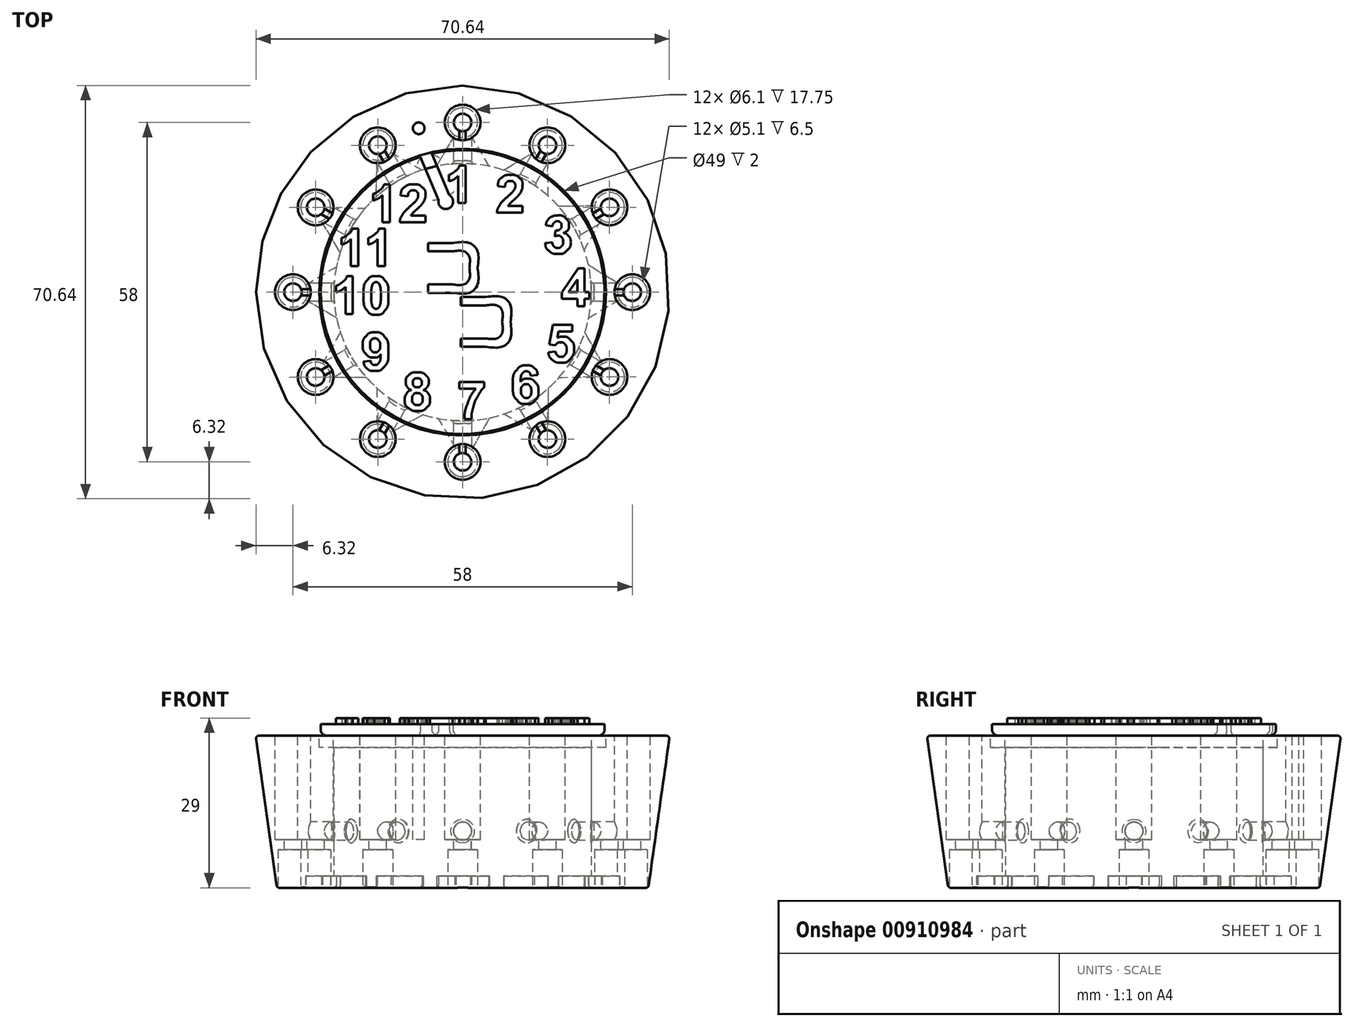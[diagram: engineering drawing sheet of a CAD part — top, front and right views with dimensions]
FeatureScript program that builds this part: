
annotation { "Feature Type Name" : "Feature", "Feature Type Description" : "" }
export const myFeature = defineFeature(function(context is Context, id is Id, definition is map)
    precondition{}
    {
        {
            var Q0;
            Q0=qCreatedBy(makeId("Front.planeOp"),FACE);
            var sketch = newSketch(context, id + "F0", { "sketchPlane" : qUnion([Q0])});
            skLineSegment(sketch, "E0.bottom", {"start": v(-22, 0) * mm, "end": v(-31.75, 0) * mm});
            skLineSegment(sketch, "E0.top", {"start": v(-22, 26) * mm, "end": v(-35.4, 26) * mm});
            skLineSegment(sketch, "E1", {"start": v(-35.4, 26) * mm, "end": v(-31.75, 0) * mm});
            skLineSegment(sketch, "E2", {"start": v(-30.25, 26.55) * mm, "end": v(-30.25, -4.35) * mm, "construction": true});
            skLineSegment(sketch, "E3", {"start": v(-22, 26) * mm, "end": v(-22, 0) * mm});
            skPoint(sketch, "E0.left.end.orphan", {"position": v(0, 26) * mm});
            skPoint(sketch, "E0.left.start.orphan", {"position": v(0, 0) * mm});
            skLineSegment(sketch, "E4", {"start": v(0, 0) * mm, "end": v(0, 33.66) * mm, "construction": true});
            skLineSegment(sketch, "E5", {"start": v(-29, 26) * mm, "end": v(-29, -2.92) * mm, "construction": true});
            skSolve(sketch);
        }
        {
            var Q0;
            Q0=makeQuery(id+"F0.imprint","IMPRINT",FACE,{"disambiguationData":[TD([[makeQuery(id+"F0.imprint","IMPRINT",EDGE,{"derivedFrom":sQuery(id+"F0.wireOp",EDGE,"E0.bottom")}),-1.0]])]});
            var Q1;
            Q1=sQuery(id+"F0.wireOp",EDGE,"E4");
            revolve(context, id + "F1", {"surfaceOperationType" : NewSurfaceOperationType.NEW, "entities" : qUnion([Q0]), "axis" : qUnion([Q1]), "revolveType" : RevolveType.FULL});
        }
        {
            var Q0;
            Q0=qCreatedBy(makeId("Top.planeOp"),FACE);
            cPlane(context, id + "F2", {"entities" : qUnion([Q0]), "cplaneType" : CPlaneType.OFFSET, "offset" : 26 * mm, "width" : 150 * mm, "height" : 150 * mm});
        }
        {
            var Q0;
            Q0=qCreatedBy(id+"F2.planeOp",FACE);
            var sketch = newSketch(context, id + "F3", { "sketchPlane" : qUnion([Q0])});
            skCircle(sketch, "E6", {"center": v(0, 0) * mm, "radius": 29 * mm, "construction": true});
            skLineSegment(sketch, "E7.0", {"start": v(-14.5, 25.11) * mm, "end": v(0, 29) * mm, "construction": true});
            skLineSegment(sketch, "E7.1", {"start": v(0, 29) * mm, "end": v(14.5, 25.11) * mm, "construction": true});
            skLineSegment(sketch, "E7.2", {"start": v(14.5, 25.11) * mm, "end": v(25.11, 14.5) * mm, "construction": true});
            skLineSegment(sketch, "E7.3", {"start": v(25.11, 14.5) * mm, "end": v(29, 0) * mm, "construction": true});
            skLineSegment(sketch, "E7.4", {"start": v(29, 0) * mm, "end": v(25.11, -14.5) * mm, "construction": true});
            skLineSegment(sketch, "E7.5", {"start": v(25.11, -14.5) * mm, "end": v(14.5, -25.11) * mm, "construction": true});
            skLineSegment(sketch, "E7.6", {"start": v(14.5, -25.11) * mm, "end": v(0, -29) * mm, "construction": true});
            skLineSegment(sketch, "E7.7", {"start": v(0, -29) * mm, "end": v(-14.5, -25.11) * mm, "construction": true});
            skLineSegment(sketch, "E7.8", {"start": v(-14.5, -25.11) * mm, "end": v(-25.11, -14.5) * mm, "construction": true});
            skLineSegment(sketch, "E7.9", {"start": v(-25.11, -14.5) * mm, "end": v(-29, 0) * mm, "construction": true});
            skLineSegment(sketch, "E7.10", {"start": v(-29, 0) * mm, "end": v(-25.11, 14.5) * mm, "construction": true});
            skLineSegment(sketch, "E7.11", {"start": v(-25.11, 14.5) * mm, "end": v(-14.5, 25.11) * mm, "construction": true});
            skCircle(sketch, "E8", {"center": v(0, 29) * mm, "radius": 3.05 * mm});
            skCircle(sketch, "E9", {"center": v(14.5, 25.11) * mm, "radius": 3.05 * mm});
            skCircle(sketch, "E10", {"center": v(-14.5, 25.11) * mm, "radius": 3.05 * mm});
            skCircle(sketch, "E11", {"center": v(-25.11, 14.5) * mm, "radius": 3.05 * mm});
            skCircle(sketch, "E12", {"center": v(25.11, 14.5) * mm, "radius": 3.05 * mm});
            skCircle(sketch, "E13", {"center": v(-29, 0) * mm, "radius": 3.05 * mm});
            skCircle(sketch, "E14", {"center": v(-25.11, -14.5) * mm, "radius": 3.05 * mm});
            skCircle(sketch, "E15", {"center": v(-14.5, -25.11) * mm, "radius": 3.05 * mm});
            skCircle(sketch, "E16", {"center": v(0, -29) * mm, "radius": 3.05 * mm});
            skCircle(sketch, "E17", {"center": v(14.5, -25.11) * mm, "radius": 3.05 * mm});
            skCircle(sketch, "E18", {"center": v(25.11, -14.5) * mm, "radius": 3.05 * mm});
            skCircle(sketch, "E19", {"center": v(29, 0) * mm, "radius": 3.05 * mm});
            skCircle(sketch, "E20", {"center": v(-7.5, 28.01) * mm, "radius": 1 * mm});
            skArc(sketch, "E21", {"start": v(0, 29) * mm, "mid": v(-7.5, 28.01) * mm, "end": v(-14.5, 25.11) * mm, "construction": true});
            skLineSegment(sketch, "E22.0", {"start": v(0.3, 24.24) * mm, "end": v(14.5, 25.11) * mm, "construction": true});
            skLineSegment(sketch, "E22.1", {"start": v(0.3, 24.24) * mm, "end": v(0, 29) * mm, "construction": true});
            skSolve(sketch);
        }
        {
            var Q0;
            Q0 = qSketchRegion(id + "F3", true);
            extrude(context, id + "F4", {"entities" : qUnion([Q0]), "operationType" : NewBodyOperationType.REMOVE, "oppositeDirection" : true, "depth" : 17.75 * mm, "offsetDistance" : 25 * mm});
        }
        {
            var Q0;
            Q0=qCreatedBy(makeId("Top.planeOp"),FACE);
            var sketch = newSketch(context, id + "F5", { "sketchPlane" : qUnion([Q0])});
            skCircle(sketch, "E23.cCircle", {"center": v(0, 0) * mm, "radius": 29 * mm, "construction": true});
            skLineSegment(sketch, "E23.0", {"start": v(0, -29) * mm, "end": v(-14.5, -25.11) * mm, "construction": true});
            skLineSegment(sketch, "E23.1", {"start": v(-14.5, -25.11) * mm, "end": v(-25.11, -14.5) * mm, "construction": true});
            skLineSegment(sketch, "E23.2", {"start": v(-25.11, -14.5) * mm, "end": v(-29, 0) * mm, "construction": true});
            skLineSegment(sketch, "E23.3", {"start": v(-29, 0) * mm, "end": v(-25.11, 14.5) * mm, "construction": true});
            skLineSegment(sketch, "E23.4", {"start": v(-25.11, 14.5) * mm, "end": v(-14.5, 25.11) * mm, "construction": true});
            skLineSegment(sketch, "E23.5", {"start": v(-14.5, 25.11) * mm, "end": v(0, 29) * mm, "construction": true});
            skLineSegment(sketch, "E23.6", {"start": v(0, 29) * mm, "end": v(14.5, 25.11) * mm, "construction": true});
            skLineSegment(sketch, "E23.7", {"start": v(14.5, 25.11) * mm, "end": v(25.11, 14.5) * mm, "construction": true});
            skLineSegment(sketch, "E23.8", {"start": v(25.11, 14.5) * mm, "end": v(29, 0) * mm, "construction": true});
            skLineSegment(sketch, "E23.9", {"start": v(29, 0) * mm, "end": v(25.11, -14.5) * mm, "construction": true});
            skLineSegment(sketch, "E23.10", {"start": v(25.11, -14.5) * mm, "end": v(14.5, -25.11) * mm, "construction": true});
            skLineSegment(sketch, "E23.11", {"start": v(14.5, -25.11) * mm, "end": v(0, -29) * mm, "construction": true});
            skCircle(sketch, "E24", {"center": v(0, -29) * mm, "radius": 2.55 * mm});
            skCircle(sketch, "E25", {"center": v(14.5, -25.11) * mm, "radius": 2.55 * mm});
            skCircle(sketch, "E26", {"center": v(-14.5, -25.11) * mm, "radius": 2.55 * mm});
            skCircle(sketch, "E27", {"center": v(25.11, -14.5) * mm, "radius": 2.55 * mm});
            skCircle(sketch, "E28", {"center": v(-25.11, -14.5) * mm, "radius": 2.55 * mm});
            skCircle(sketch, "E29", {"center": v(0, 29) * mm, "radius": 2.55 * mm});
            skCircle(sketch, "E30", {"center": v(-14.5, 25.11) * mm, "radius": 2.55 * mm});
            skCircle(sketch, "E31", {"center": v(14.5, 25.11) * mm, "radius": 2.55 * mm});
            skCircle(sketch, "E32", {"center": v(25.11, 14.5) * mm, "radius": 2.55 * mm});
            skCircle(sketch, "E33", {"center": v(29, 0) * mm, "radius": 2.55 * mm});
            skCircle(sketch, "E34", {"center": v(-25.11, 14.5) * mm, "radius": 2.55 * mm});
            skCircle(sketch, "E35", {"center": v(-29, 0) * mm, "radius": 2.55 * mm});
            skSolve(sketch);
        }
        {
            var Q0;
            Q0 = qSketchRegion(id + "F5", true);
            extrude(context, id + "F6", {"entities" : qUnion([Q0]), "operationType" : NewBodyOperationType.REMOVE, "depth" : 6.5 * mm, "offsetDistance" : 25 * mm});
        }
        {
            var Q0;
            Q0=qCreatedBy(id+"F2.planeOp",FACE);
            var sketch = newSketch(context, id + "F7", { "sketchPlane" : qUnion([Q0])});
            skCircle(sketch, "E36.cCircle", {"center": v(0, 0) * mm, "radius": 29 * mm, "construction": true});
            skLineSegment(sketch, "E36.0", {"start": v(0, 29) * mm, "end": v(14.5, 25.11) * mm, "construction": true});
            skLineSegment(sketch, "E36.1", {"start": v(14.5, 25.11) * mm, "end": v(25.12, 14.5) * mm, "construction": true});
            skLineSegment(sketch, "E36.2", {"start": v(25.12, 14.5) * mm, "end": v(29, 0) * mm, "construction": true});
            skLineSegment(sketch, "E36.3", {"start": v(29, 0) * mm, "end": v(25.11, -14.5) * mm, "construction": true});
            skLineSegment(sketch, "E36.4", {"start": v(25.11, -14.5) * mm, "end": v(14.5, -25.12) * mm, "construction": true});
            skLineSegment(sketch, "E36.5", {"start": v(14.5, -25.12) * mm, "end": v(0, -29) * mm, "construction": true});
            skLineSegment(sketch, "E36.6", {"start": v(0, -29) * mm, "end": v(-14.5, -25.11) * mm, "construction": true});
            skLineSegment(sketch, "E36.7", {"start": v(-14.5, -25.11) * mm, "end": v(-25.12, -14.5) * mm, "construction": true});
            skLineSegment(sketch, "E36.8", {"start": v(-25.12, -14.5) * mm, "end": v(-29, 0) * mm, "construction": true});
            skLineSegment(sketch, "E36.9", {"start": v(-29, 0) * mm, "end": v(-25.11, 14.5) * mm, "construction": true});
            skLineSegment(sketch, "E36.10", {"start": v(-25.11, 14.5) * mm, "end": v(-14.5, 25.12) * mm, "construction": true});
            skLineSegment(sketch, "E36.11", {"start": v(-14.5, 25.12) * mm, "end": v(0, 29) * mm, "construction": true});
            skCircle(sketch, "E37", {"center": v(14.5, 25.11) * mm, "radius": 1.5 * mm});
            skCircle(sketch, "E38", {"center": v(-14.5, 25.12) * mm, "radius": 1.5 * mm});
            skCircle(sketch, "E39", {"center": v(25.12, 14.5) * mm, "radius": 1.5 * mm});
            skCircle(sketch, "E40", {"center": v(0, 29) * mm, "radius": 1.5 * mm});
            skCircle(sketch, "E41", {"center": v(-25.11, 14.5) * mm, "radius": 1.5 * mm});
            skCircle(sketch, "E42", {"center": v(-29, 0) * mm, "radius": 1.5 * mm});
            skCircle(sketch, "E43", {"center": v(-25.12, -14.5) * mm, "radius": 1.5 * mm});
            skCircle(sketch, "E44", {"center": v(-14.5, -25.11) * mm, "radius": 1.5 * mm});
            skCircle(sketch, "E45", {"center": v(0, -29) * mm, "radius": 1.5 * mm});
            skCircle(sketch, "E46", {"center": v(14.5, -25.12) * mm, "radius": 1.5 * mm});
            skCircle(sketch, "E47", {"center": v(25.11, -14.5) * mm, "radius": 1.5 * mm});
            skCircle(sketch, "E48", {"center": v(29, 0) * mm, "radius": 1.5 * mm});
            skSolve(sketch);
        }
        {
            var Q0;
            Q0 = qSketchRegion(id + "F7", true);
            extrude(context, id + "F8", {"entities" : qUnion([Q0]), "operationType" : NewBodyOperationType.REMOVE, "oppositeDirection" : true, "depth" : 30 * mm, "offsetDistance" : 25 * mm});
        }
        {
            var Q0;
            Q0=qCreatedBy(makeId("Right.planeOp"),FACE);
            var sketch = newSketch(context, id + "F9", { "sketchPlane" : qUnion([Q0])});
            skCircle(sketch, "E49", {"center": v(0, 9.7) * mm, "radius": 1.55 * mm});
            skSolve(sketch);
        }
        {
            var Q0;
            Q0=makeQuery(id+"F9.imprint","IMPRINT",FACE,{"disambiguationData":[TD([[makeQuery(id+"F9.imprint","IMPRINT",EDGE,{"derivedFrom":sQuery(id+"F9.wireOp",EDGE,"E49")}),1.0]])]});
            extrude(context, id + "F10", {"entities" : qUnion([Q0]), "operationType" : NewBodyOperationType.REMOVE, "depth" : 29 * mm, "offsetDistance" : 25 * mm, "hasSecondDirection" : true, "secondDirectionOppositeDirection" : true, "secondDirectionDepth" : 29 * mm});
        }
        {
            var Q0;
            Q0=qCreatedBy(makeId("Front.planeOp"),FACE);
            var sketch = newSketch(context, id + "F11", { "sketchPlane" : qUnion([Q0])});
            skCircle(sketch, "E50", {"center": v(0, 9.7) * mm, "radius": 1.55 * mm});
            skSolve(sketch);
        }
        {
            var Q0;
            Q0=makeQuery(id+"F11.imprint","IMPRINT",FACE,{"disambiguationData":[TD([[makeQuery(id+"F11.imprint","IMPRINT",EDGE,{"derivedFrom":sQuery(id+"F11.wireOp",EDGE,"E50")}),1.0]])]});
            var Q1;
            Q1=sQuery(id+"F11.wireOp",EDGE,"E50");
            extrude(context, id + "F12", {"entities" : qUnion([Q0]), "operationType" : NewBodyOperationType.REMOVE, "surfaceEntities" : qUnion([Q1]), "oppositeDirection" : true, "depth" : 29 * mm, "offsetDistance" : 25 * mm, "hasSecondDirection" : true, "secondDirectionOppositeDirection" : false, "secondDirectionDepth" : 29 * mm});
        }
        {
            var Q0;
            Q0=makeQuery(id+"F1.opRevolve","SWEPT_FACE",FACE,{"disambiguationData":[OSD([sQuery(id+"F0.wireOp",EDGE,"E3")])]});
            cPlane(context, id + "F13", {"entities" : qUnion([Q0]), "cplaneType" : CPlaneType.LINE_ANGLE, "offset" : 25 * mm, "angle" : 60 * degree, "width" : 150 * mm, "height" : 150 * mm});
        }
        {
            var Q0;
            Q0=makeQuery(id+"F1.opRevolve","SWEPT_FACE",FACE,{"disambiguationData":[OSD([sQuery(id+"F0.wireOp",EDGE,"E1")])]});
            cPlane(context, id + "F14", {"entities" : qUnion([Q0]), "cplaneType" : CPlaneType.LINE_ANGLE, "offset" : 25 * mm, "angle" : 30 * degree, "width" : 150 * mm, "height" : 150 * mm});
        }
        {
            var Q0;
            Q0=qCreatedBy(id+"F13.planeOp",FACE);
            var sketch = newSketch(context, id + "F15", { "sketchPlane" : qUnion([Q0])});
            skCircle(sketch, "E51", {"center": v(0, 9.7) * mm, "radius": 1.55 * mm});
            skSolve(sketch);
        }
        {
            var Q0;
            Q0=makeQuery(id+"F15.imprint","IMPRINT",FACE,{"disambiguationData":[TD([[makeQuery(id+"F15.imprint","IMPRINT",EDGE,{"derivedFrom":sQuery(id+"F15.wireOp",EDGE,"E51")}),1.0]])]});
            var Q1;
            Q1=sQuery(id+"F15.wireOp",EDGE,"E51");
            extrude(context, id + "F16", {"entities" : qUnion([Q0]), "operationType" : NewBodyOperationType.REMOVE, "surfaceEntities" : qUnion([Q1]), "oppositeDirection" : true, "depth" : 29 * mm, "offsetDistance" : 25 * mm, "hasSecondDirection" : true, "secondDirectionOppositeDirection" : false, "secondDirectionDepth" : 29 * mm});
        }
        {
            var Q0;
            Q0=qCreatedBy(id+"F14.planeOp",FACE);
            var sketch = newSketch(context, id + "F17", { "sketchPlane" : qUnion([Q0])});
            skCircle(sketch, "E52", {"center": v(0, 9.7) * mm, "radius": 1.55 * mm});
            skSolve(sketch);
        }
        {
            var Q0;
            Q0=makeQuery(id+"F17.imprint","IMPRINT",FACE,{"disambiguationData":[TD([[makeQuery(id+"F17.imprint","IMPRINT",EDGE,{"derivedFrom":sQuery(id+"F17.wireOp",EDGE,"E52")}),1.0]])]});
            var Q1;
            Q1=sQuery(id+"F17.wireOp",EDGE,"E52");
            extrude(context, id + "F18", {"entities" : qUnion([Q0]), "operationType" : NewBodyOperationType.REMOVE, "surfaceEntities" : qUnion([Q1]), "oppositeDirection" : true, "depth" : 29 * mm, "offsetDistance" : 25 * mm, "hasSecondDirection" : true, "secondDirectionOppositeDirection" : false, "secondDirectionDepth" : 29 * mm});
        }
        {
            var Q0;
            Q0=makeQuery(id+"F1.opRevolve","SWEPT_FACE",FACE,{"disambiguationData":[OSD([sQuery(id+"F0.wireOp",EDGE,"E1")])]});
            cPlane(context, id + "F19", {"entities" : qUnion([Q0]), "cplaneType" : CPlaneType.LINE_ANGLE, "offset" : 25 * mm, "angle" : 30 * degree, "oppositeDirection" : true, "width" : 150 * mm, "height" : 150 * mm});
        }
        {
            var Q0;
            Q0=makeQuery(id+"F1.opRevolve","SWEPT_FACE",FACE,{"disambiguationData":[OSD([sQuery(id+"F0.wireOp",EDGE,"E1")])]});
            cPlane(context, id + "F20", {"entities" : qUnion([Q0]), "cplaneType" : CPlaneType.LINE_ANGLE, "offset" : 25 * mm, "angle" : 60 * degree, "oppositeDirection" : true, "width" : 150 * mm, "height" : 150 * mm});
        }
        {
            var Q0;
            Q0=qCreatedBy(id+"F19.planeOp",FACE);
            var sketch = newSketch(context, id + "F21", { "sketchPlane" : qUnion([Q0])});
            skCircle(sketch, "E53", {"center": v(0, 9.7) * mm, "radius": 1.55 * mm});
            skSolve(sketch);
        }
        {
            var Q0;
            Q0=qCreatedBy(id+"F20.planeOp",FACE);
            var sketch = newSketch(context, id + "F22", { "sketchPlane" : qUnion([Q0])});
            skCircle(sketch, "E54", {"center": v(0, 9.7) * mm, "radius": 1.55 * mm});
            skSolve(sketch);
        }
        {
            var Q0;
            Q0 = qSketchRegion(id + "F22", true);
            extrude(context, id + "F23", {"entities" : qUnion([Q0]), "operationType" : NewBodyOperationType.REMOVE, "oppositeDirection" : true, "depth" : 29 * mm, "offsetDistance" : 25 * mm, "hasSecondDirection" : true, "secondDirectionOppositeDirection" : false, "secondDirectionDepth" : 29 * mm});
        }
        {
            var Q0;
            Q0 = qSketchRegion(id + "F21", true);
            extrude(context, id + "F24", {"entities" : qUnion([Q0]), "operationType" : NewBodyOperationType.REMOVE, "oppositeDirection" : true, "depth" : 29 * mm, "offsetDistance" : 25 * mm, "hasSecondDirection" : true, "secondDirectionOppositeDirection" : false, "secondDirectionDepth" : 29 * mm});
        }
        {
            var Q0;
            Q0=qCreatedBy(id+"F2.planeOp",FACE);
            var sketch = newSketch(context, id + "F25", { "sketchPlane" : qUnion([Q0])});
            skCircle(sketch, "E55", {"center": v(0, 0) * mm, "radius": 24.5 * mm});
            skSolve(sketch);
        }
        {
            var Q0;
            Q0 = qSketchRegion(id + "F25", true);
            extrude(context, id + "F26", {"entities" : qUnion([Q0]), "operationType" : NewBodyOperationType.REMOVE, "oppositeDirection" : true, "depth" : 2 * mm, "offsetDistance" : 25 * mm});
        }
        {
            var Q0;
            Q0=makeQuery(id+"F6.boolean.opBoolean","COPY",EDGE,{"derivedFrom":makeQuery(id+"F6.opExtrude","CAP_EDGE",EDGE,{"disambiguationData":[OSD([sQuery(id+"F5.wireOp",EDGE,"E27")])],"isStart":true})});
            var Q1;
            Q1=makeQuery(id+"F6.boolean.opBoolean","COPY",EDGE,{"derivedFrom":makeQuery(id+"F6.opExtrude","CAP_EDGE",EDGE,{"disambiguationData":[OSD([sQuery(id+"F5.wireOp",EDGE,"E25")])],"isStart":true})});
            var Q2;
            Q2=makeQuery(id+"F1.opRevolve","SWEPT_EDGE",EDGE,{"disambiguationData":[OSD([sQuery(id+"F0.wireOp",EDGE,"E0.bottom"),sQuery(id+"F0.wireOp",EDGE,"E1")])]});
            var Q3;
            Q3=makeQuery(id+"F6.boolean.opBoolean","COPY",EDGE,{"derivedFrom":makeQuery(id+"F6.opExtrude","CAP_EDGE",EDGE,{"disambiguationData":[OSD([sQuery(id+"F5.wireOp",EDGE,"E32")])],"isStart":true})});
            var Q4;
            Q4=makeQuery(id+"F6.boolean.opBoolean","COPY",EDGE,{"derivedFrom":makeQuery(id+"F6.opExtrude","CAP_EDGE",EDGE,{"disambiguationData":[OSD([sQuery(id+"F5.wireOp",EDGE,"E33")])],"isStart":true})});
            var Q5;
            Q5=makeQuery(id+"F6.boolean.opBoolean","COPY",EDGE,{"derivedFrom":makeQuery(id+"F6.opExtrude","CAP_EDGE",EDGE,{"disambiguationData":[OSD([sQuery(id+"F5.wireOp",EDGE,"E31")])],"isStart":true})});
            var Q6;
            Q6=makeQuery(id+"F6.boolean.opBoolean","COPY",EDGE,{"derivedFrom":makeQuery(id+"F6.opExtrude","CAP_EDGE",EDGE,{"disambiguationData":[OSD([sQuery(id+"F5.wireOp",EDGE,"E29")])],"isStart":true})});
            var Q7;
            Q7=makeQuery(id+"F6.boolean.opBoolean","COPY",EDGE,{"derivedFrom":makeQuery(id+"F6.opExtrude","CAP_EDGE",EDGE,{"disambiguationData":[OSD([sQuery(id+"F5.wireOp",EDGE,"E30")])],"isStart":true})});
            var Q8;
            Q8=makeQuery(id+"F6.boolean.opBoolean","COPY",EDGE,{"derivedFrom":makeQuery(id+"F6.opExtrude","CAP_EDGE",EDGE,{"disambiguationData":[OSD([sQuery(id+"F5.wireOp",EDGE,"E34")])],"isStart":true})});
            var Q9;
            Q9=makeQuery(id+"F6.boolean.opBoolean","COPY",EDGE,{"derivedFrom":makeQuery(id+"F6.opExtrude","CAP_EDGE",EDGE,{"disambiguationData":[OSD([sQuery(id+"F5.wireOp",EDGE,"E35")])],"isStart":true})});
            var Q10;
            Q10=makeQuery(id+"F6.boolean.opBoolean","COPY",EDGE,{"derivedFrom":makeQuery(id+"F6.opExtrude","CAP_EDGE",EDGE,{"disambiguationData":[OSD([sQuery(id+"F5.wireOp",EDGE,"E28")])],"isStart":true})});
            var Q11;
            Q11=makeQuery(id+"F6.boolean.opBoolean","COPY",EDGE,{"derivedFrom":makeQuery(id+"F6.opExtrude","CAP_EDGE",EDGE,{"disambiguationData":[OSD([sQuery(id+"F5.wireOp",EDGE,"E26")])],"isStart":true})});
            var Q12;
            Q12=makeQuery(id+"F6.boolean.opBoolean","COPY",EDGE,{"derivedFrom":makeQuery(id+"F6.opExtrude","CAP_EDGE",EDGE,{"disambiguationData":[OSD([sQuery(id+"F5.wireOp",EDGE,"E24")])],"isStart":true})});
            var Q13;
            Q13=makeQuery(id+"F1.opRevolve","SWEPT_EDGE",EDGE,{"disambiguationData":[OSD([sQuery(id+"F0.wireOp",EDGE,"E0.bottom"),sQuery(id+"F0.wireOp",EDGE,"E3")])]});
            var Q14;
            Q14=makeQuery(id+"F1.opRevolve","SWEPT_EDGE",EDGE,{"disambiguationData":[OSD([sQuery(id+"F0.wireOp",EDGE,"E0.top"),sQuery(id+"F0.wireOp",EDGE,"E1")])]});
            var Q15;
            Q15=makeQuery(id+"F4.boolean.opBoolean","COPY",EDGE,{"derivedFrom":makeQuery(id+"F4.opExtrude","CAP_EDGE",EDGE,{"disambiguationData":[OSD([sQuery(id+"F3.wireOp",EDGE,"E15")])],"isStart":true})});
            var Q16;
            Q16=makeQuery(id+"F4.boolean.opBoolean","COPY",EDGE,{"derivedFrom":makeQuery(id+"F4.opExtrude","CAP_EDGE",EDGE,{"disambiguationData":[OSD([sQuery(id+"F3.wireOp",EDGE,"E14")])],"isStart":true})});
            var Q17;
            Q17=makeQuery(id+"F4.boolean.opBoolean","COPY",EDGE,{"derivedFrom":makeQuery(id+"F4.opExtrude","CAP_EDGE",EDGE,{"disambiguationData":[OSD([sQuery(id+"F3.wireOp",EDGE,"E16")])],"isStart":true})});
            var Q18;
            Q18=makeQuery(id+"F4.boolean.opBoolean","COPY",EDGE,{"derivedFrom":makeQuery(id+"F4.opExtrude","CAP_EDGE",EDGE,{"disambiguationData":[OSD([sQuery(id+"F3.wireOp",EDGE,"E17")])],"isStart":true})});
            var Q19;
            Q19=makeQuery(id+"F4.boolean.opBoolean","COPY",EDGE,{"derivedFrom":makeQuery(id+"F4.opExtrude","CAP_EDGE",EDGE,{"disambiguationData":[OSD([sQuery(id+"F3.wireOp",EDGE,"E18")])],"isStart":true})});
            var Q20;
            Q20=makeQuery(id+"F4.boolean.opBoolean","COPY",EDGE,{"derivedFrom":makeQuery(id+"F4.opExtrude","CAP_EDGE",EDGE,{"disambiguationData":[OSD([sQuery(id+"F3.wireOp",EDGE,"E19")])],"isStart":true})});
            var Q21;
            Q21=makeQuery(id+"F4.boolean.opBoolean","COPY",EDGE,{"derivedFrom":makeQuery(id+"F4.opExtrude","CAP_EDGE",EDGE,{"disambiguationData":[OSD([sQuery(id+"F3.wireOp",EDGE,"E12")])],"isStart":true})});
            var Q22;
            Q22=makeQuery(id+"F4.boolean.opBoolean","COPY",EDGE,{"derivedFrom":makeQuery(id+"F4.opExtrude","CAP_EDGE",EDGE,{"disambiguationData":[OSD([sQuery(id+"F3.wireOp",EDGE,"E10")])],"isStart":true})});
            var Q23;
            Q23=makeQuery(id+"F4.boolean.opBoolean","COPY",EDGE,{"derivedFrom":makeQuery(id+"F4.opExtrude","CAP_EDGE",EDGE,{"disambiguationData":[OSD([sQuery(id+"F3.wireOp",EDGE,"E9")])],"isStart":true})});
            var Q24;
            Q24=makeQuery(id+"F4.boolean.opBoolean","COPY",EDGE,{"derivedFrom":makeQuery(id+"F4.opExtrude","CAP_EDGE",EDGE,{"disambiguationData":[OSD([sQuery(id+"F3.wireOp",EDGE,"E8")])],"isStart":true})});
            var Q25;
            Q25=makeQuery(id+"F4.boolean.opBoolean","COPY",EDGE,{"derivedFrom":makeQuery(id+"F4.opExtrude","CAP_EDGE",EDGE,{"disambiguationData":[OSD([sQuery(id+"F3.wireOp",EDGE,"E13")])],"isStart":true})});
            var Q26;
            Q26=makeQuery(id+"F4.boolean.opBoolean","COPY",EDGE,{"derivedFrom":makeQuery(id+"F4.opExtrude","CAP_EDGE",EDGE,{"disambiguationData":[OSD([sQuery(id+"F3.wireOp",EDGE,"E11")])],"isStart":true})});
            var Q27;
            Q27=makeQuery(id+"F16.boolean.opBoolean","INTERSECT",EDGE,{"disambiguationData":[OD(1.0)],"derivedFrom":[makeQuery(id+"F1.opRevolve","SWEPT_FACE",FACE,{"disambiguationData":[OSD([sQuery(id+"F0.wireOp",EDGE,"E3")])]}),makeQuery(id+"F16.opExtrude","SWEPT_FACE",FACE,{"disambiguationData":[OSD([sQuery(id+"F15.wireOp",EDGE,"E51")])]})]});
            var Q28;
            Q28=makeQuery(id+"F12.boolean.opBoolean","INTERSECT",EDGE,{"disambiguationData":[OD(1.0)],"derivedFrom":[makeQuery(id+"F1.opRevolve","SWEPT_FACE",FACE,{"disambiguationData":[OSD([sQuery(id+"F0.wireOp",EDGE,"E3")])]}),makeQuery(id+"F12.opExtrude","SWEPT_FACE",FACE,{"disambiguationData":[OSD([sQuery(id+"F11.wireOp",EDGE,"E50")])]})]});
            var Q29;
            Q29=makeQuery(id+"F23.boolean.opBoolean","INTERSECT",EDGE,{"disambiguationData":[OD(1.0)],"derivedFrom":[makeQuery(id+"F1.opRevolve","SWEPT_FACE",FACE,{"disambiguationData":[OSD([sQuery(id+"F0.wireOp",EDGE,"E3")])]}),makeQuery(id+"F23.opExtrude","SWEPT_FACE",FACE,{"disambiguationData":[OSD([sQuery(id+"F22.wireOp",EDGE,"E54")])]})]});
            var Q30;
            Q30=makeQuery(id+"F18.boolean.opBoolean","INTERSECT",EDGE,{"disambiguationData":[OD(1.0)],"derivedFrom":[makeQuery(id+"F1.opRevolve","SWEPT_FACE",FACE,{"disambiguationData":[OSD([sQuery(id+"F0.wireOp",EDGE,"E3")])]}),makeQuery(id+"F18.opExtrude","SWEPT_FACE",FACE,{"disambiguationData":[OSD([sQuery(id+"F17.wireOp",EDGE,"E52")])]})]});
            var Q31;
            Q31=makeQuery(id+"F24.boolean.opBoolean","INTERSECT",EDGE,{"disambiguationData":[OD(1.0)],"derivedFrom":[makeQuery(id+"F1.opRevolve","SWEPT_FACE",FACE,{"disambiguationData":[OSD([sQuery(id+"F0.wireOp",EDGE,"E3")])]}),makeQuery(id+"F24.opExtrude","SWEPT_FACE",FACE,{"disambiguationData":[OSD([sQuery(id+"F21.wireOp",EDGE,"E53")])]})]});
            var Q32;
            Q32=makeQuery(id+"F10.boolean.opBoolean","INTERSECT",EDGE,{"disambiguationData":[OD(1.0)],"derivedFrom":[makeQuery(id+"F1.opRevolve","SWEPT_FACE",FACE,{"disambiguationData":[OSD([sQuery(id+"F0.wireOp",EDGE,"E3")])]}),makeQuery(id+"F10.opExtrude","SWEPT_FACE",FACE,{"disambiguationData":[OSD([sQuery(id+"F9.wireOp",EDGE,"E49")])]})]});
            var Q33;
            Q33=makeQuery(id+"F16.boolean.opBoolean","INTERSECT",EDGE,{"disambiguationData":[OD(0.0)],"derivedFrom":[makeQuery(id+"F1.opRevolve","SWEPT_FACE",FACE,{"disambiguationData":[OSD([sQuery(id+"F0.wireOp",EDGE,"E3")])]}),makeQuery(id+"F16.opExtrude","SWEPT_FACE",FACE,{"disambiguationData":[OSD([sQuery(id+"F15.wireOp",EDGE,"E51")])]})]});
            var Q34;
            Q34=makeQuery(id+"F12.boolean.opBoolean","INTERSECT",EDGE,{"disambiguationData":[OD(0.0)],"derivedFrom":[makeQuery(id+"F1.opRevolve","SWEPT_FACE",FACE,{"disambiguationData":[OSD([sQuery(id+"F0.wireOp",EDGE,"E3")])]}),makeQuery(id+"F12.opExtrude","SWEPT_FACE",FACE,{"disambiguationData":[OSD([sQuery(id+"F11.wireOp",EDGE,"E50")])]})]});
            var Q35;
            Q35=makeQuery(id+"F23.boolean.opBoolean","INTERSECT",EDGE,{"disambiguationData":[OD(0.0)],"derivedFrom":[makeQuery(id+"F1.opRevolve","SWEPT_FACE",FACE,{"disambiguationData":[OSD([sQuery(id+"F0.wireOp",EDGE,"E3")])]}),makeQuery(id+"F23.opExtrude","SWEPT_FACE",FACE,{"disambiguationData":[OSD([sQuery(id+"F22.wireOp",EDGE,"E54")])]})]});
            var Q36;
            Q36=makeQuery(id+"F18.boolean.opBoolean","INTERSECT",EDGE,{"disambiguationData":[OD(0.0)],"derivedFrom":[makeQuery(id+"F1.opRevolve","SWEPT_FACE",FACE,{"disambiguationData":[OSD([sQuery(id+"F0.wireOp",EDGE,"E3")])]}),makeQuery(id+"F18.opExtrude","SWEPT_FACE",FACE,{"disambiguationData":[OSD([sQuery(id+"F17.wireOp",EDGE,"E52")])]})]});
            var Q37;
            Q37=makeQuery(id+"F10.boolean.opBoolean","INTERSECT",EDGE,{"disambiguationData":[OD(0.0)],"derivedFrom":[makeQuery(id+"F1.opRevolve","SWEPT_FACE",FACE,{"disambiguationData":[OSD([sQuery(id+"F0.wireOp",EDGE,"E3")])]}),makeQuery(id+"F10.opExtrude","SWEPT_FACE",FACE,{"disambiguationData":[OSD([sQuery(id+"F9.wireOp",EDGE,"E49")])]})]});
            var Q38;
            Q38=makeQuery(id+"F24.boolean.opBoolean","INTERSECT",EDGE,{"disambiguationData":[OD(0.0)],"derivedFrom":[makeQuery(id+"F1.opRevolve","SWEPT_FACE",FACE,{"disambiguationData":[OSD([sQuery(id+"F0.wireOp",EDGE,"E3")])]}),makeQuery(id+"F24.opExtrude","SWEPT_FACE",FACE,{"disambiguationData":[OSD([sQuery(id+"F21.wireOp",EDGE,"E53")])]})]});
            var Q39;
            Q39=makeQuery(id+"F4.boolean.opBoolean","COPY",EDGE,{"derivedFrom":makeQuery(id+"F4.opExtrude","CAP_EDGE",EDGE,{"disambiguationData":[OSD([sQuery(id+"F3.wireOp",EDGE,"E20")])],"isStart":true})});
            var Q40;
            Q40=makeQuery(id+"F26.boolean.opBoolean","COPY",EDGE,{"derivedFrom":makeQuery(id+"F26.opExtrude","CAP_EDGE",EDGE,{"disambiguationData":[OSD([sQuery(id+"F25.wireOp",EDGE,"E55")])],"isStart":true})});
            fillet(context, id + "F27", {"entities" : qUnion([Q0, Q1, Q2, Q3, Q4, Q5, Q6, Q7, Q8, Q9, Q10, Q11, Q12, Q13, Q14, Q15, Q16, Q17, Q18, Q19, Q20, Q21, Q22, Q23, Q24, Q25, Q26, Q27, Q28, Q29, Q30, Q31, Q32, Q33, Q34, Q35, Q36, Q37, Q38, Q39, Q40]), "radius" : 0.5 * mm, "tangentPropagation" : true, "allowEdgeOverflow" : false});
        }
        {
            var Q0;
            Q0=qCreatedBy(makeId("Top.planeOp"),FACE);
            var sketch = newSketch(context, id + "F28", { "sketchPlane" : qUnion([Q0])});
            skCircle(sketch, "E56.cCircle", {"center": v(0, 0) * mm, "radius": 29.11 * mm, "construction": true});
            skLineSegment(sketch, "E56.0", {"start": v(0, 29.11) * mm, "end": v(5.4, 19.96) * mm});
            skLineSegment(sketch, "E56.1", {"start": v(25.21, -14.56) * mm, "end": v(14.58, -14.66) * mm});
            skLineSegment(sketch, "E56.2", {"start": v(-25.21, -14.56) * mm, "end": v(-19.99, -5.3) * mm});
            skLineSegment(sketch, "E57.0", {"start": v(14.51, 25.24) * mm, "end": v(14.53, 14.71) * mm});
            skLineSegment(sketch, "E57.1", {"start": v(14.6, -25.19) * mm, "end": v(5.48, -19.94) * mm});
            skLineSegment(sketch, "E57.2", {"start": v(-29.11, -0.05) * mm, "end": v(-20, 5.23) * mm});
            skLineSegment(sketch, "E58.0", {"start": v(25.05, 14.82) * mm, "end": v(19.89, 5.65) * mm});
            skLineSegment(sketch, "E58.1", {"start": v(0.31, -29.1) * mm, "end": v(-5.05, -20.05) * mm});
            skLineSegment(sketch, "E58.2", {"start": v(-25.37, 14.29) * mm, "end": v(-14.84, 14.4) * mm});
            skLineSegment(sketch, "E59.0", {"start": v(29.11, 0) * mm, "end": v(19.97, -5.35) * mm});
            skLineSegment(sketch, "E59.1", {"start": v(-14.56, -25.21) * mm, "end": v(-14.62, -14.62) * mm});
            skLineSegment(sketch, "E59.2", {"start": v(-14.56, 25.21) * mm, "end": v(-5.35, 19.97) * mm});
            skLineSegment(sketch, "E60.trimOffspring", {"start": v(5.4, 19.96) * mm, "end": v(14.51, 25.24) * mm});
            skLineSegment(sketch, "E61.trimOffspring", {"start": v(14.53, 14.71) * mm, "end": v(25.05, 14.82) * mm});
            skLineSegment(sketch, "E62.trimOffspring", {"start": v(19.89, 5.65) * mm, "end": v(29.11, 0) * mm});
            skLineSegment(sketch, "E63.trimOffspring", {"start": v(19.97, -5.35) * mm, "end": v(25.21, -14.56) * mm});
            skLineSegment(sketch, "E64.trimOffspring", {"start": v(14.58, -14.66) * mm, "end": v(14.6, -25.19) * mm});
            skLineSegment(sketch, "E65.trimOffspring", {"start": v(5.48, -19.94) * mm, "end": v(0.31, -29.1) * mm});
            skLineSegment(sketch, "E66.trimOffspring", {"start": v(-19.99, -5.3) * mm, "end": v(-29.11, -0.05) * mm});
            skLineSegment(sketch, "E67.trimOffspring", {"start": v(-5.05, -20.05) * mm, "end": v(-14.56, -25.21) * mm});
            skLineSegment(sketch, "E68.trimOffspring", {"start": v(-14.62, -14.62) * mm, "end": v(-25.21, -14.56) * mm});
            skLineSegment(sketch, "E69.trimOffspring", {"start": v(-20, 5.23) * mm, "end": v(-25.37, 14.29) * mm});
            skLineSegment(sketch, "E70.trimOffspring", {"start": v(-14.84, 14.4) * mm, "end": v(-14.56, 25.21) * mm});
            skLineSegment(sketch, "E71.trimOffspring", {"start": v(-5.35, 19.97) * mm, "end": v(0, 29.11) * mm});
            skCircle(sketch, "E72", {"center": v(0, 0) * mm, "radius": 20.68 * mm});
            skSolve(sketch);
        }
        {
            var Q0;
            Q0 = qSketchRegion(id + "F28", true);
            extrude(context, id + "F29", {"entities" : qUnion([Q0]), "operationType" : NewBodyOperationType.REMOVE, "depth" : 2 * mm, "offsetDistance" : 25 * mm});
        }
        {
            var Q0;
            Q0=qCreatedBy(id+"F2.planeOp",FACE);
            var sketch = newSketch(context, id + "F30", { "sketchPlane" : qUnion([Q0])});
            skArc(sketch, "E73", {"start": v(-7.2, 23.15) * mm, "mid": v(6.23, -23.43) * mm, "end": v(-5.25, 23.67) * mm});
            skLineSegment(sketch, "E74", {"start": v(-7.2, 23.15) * mm, "end": v(-4.1, 15.78) * mm});
            skPoint(sketch, "E75.endSnap0", {"position": v(-5.26, 18.55) * mm});
            skLineSegment(sketch, "E76", {"start": v(-2.25, 16.56) * mm, "end": v(-4.1, 15.78) * mm, "construction": true});
            skArc(sketch, "E77", {"start": v(-4.1, 15.78) * mm, "mid": v(-2.39, 14.31) * mm, "end": v(-2.25, 16.56) * mm});
            skLineSegment(sketch, "E78.trimOffspring", {"start": v(-2.25, 16.56) * mm, "end": v(-5.26, 23.7) * mm});
            skPoint(sketch, "E79.orphan", {"position": v(-1.47, 14.72) * mm});
            skPoint(sketch, "E80.orphan", {"position": v(-3.32, 13.94) * mm});
            skSolve(sketch);
        }
        {
            var Q0;
            Q0 = qSketchRegion(id + "F30", true);
            extrude(context, id + "F31", {"entities" : qUnion([Q0]), "depth" : 2 * mm, "offsetDistance" : 25 * mm});
        }
        {
            var Q0;
            Q0=makeQuery(id+"F31.opExtrude","CAP_FACE",FACE,{"disambiguationData":[OSD([sQuery(id+"F30.wireOp",EDGE,"E73"),sQuery(id+"F30.wireOp",EDGE,"E74"),sQuery(id+"F30.wireOp",EDGE,"E77"),sQuery(id+"F30.wireOp",EDGE,"E78.trimOffspring")])],"isStart":false});
            var sketch = newSketch(context, id + "F32", { "sketchPlane" : qUnion([Q0])});
            skLineSegment(sketch, "E81", {"start": v(12.83, -14.13) * mm, "end": v(11.62, -14.26) * mm});
            skLineSegment(sketch, "E82", {"start": v(0.5, 15.23) * mm, "end": v(-0.76, 15.23) * mm});
            skLineSegment(sketch, "E83", {"start": v(-0.76, 15.23) * mm, "end": v(-0.76, 19.88) * mm});
            skLineSegment(sketch, "E84", {"start": v(-2.37, 18.94) * mm, "end": v(-2.37, 20.06) * mm});
            skLineSegment(sketch, "E85", {"start": v(-0.52, 21.7) * mm, "end": v(0.5, 21.7) * mm});
            skLineSegment(sketch, "E86", {"start": v(0.5, 21.7) * mm, "end": v(0.5, 15.23) * mm});
            skLineSegment(sketch, "E87", {"start": v(10.24, 14.72) * mm, "end": v(10.24, 13.58) * mm});
            skLineSegment(sketch, "E88", {"start": v(10.24, 13.58) * mm, "end": v(5.87, 13.58) * mm});
            skLineSegment(sketch, "E89", {"start": v(7.26, 18) * mm, "end": v(6.02, 18.13) * mm});
            skLineSegment(sketch, "E90", {"start": v(7.77, 14.72) * mm, "end": v(10.24, 14.72) * mm});
            skLineSegment(sketch, "E91", {"start": v(14.13, 8.36) * mm, "end": v(15.34, 8.5) * mm});
            skLineSegment(sketch, "E92", {"start": v(15.73, 9.56) * mm, "end": v(15.87, 10.56) * mm});
            skLineSegment(sketch, "E93", {"start": v(15.37, 11.24) * mm, "end": v(14.22, 11.44) * mm});
            skLineSegment(sketch, "E94", {"start": v(19.62, -2.4) * mm, "end": v(19.62, -1.1) * mm});
            skLineSegment(sketch, "E95", {"start": v(19.62, -1.1) * mm, "end": v(16.96, -1.1) * mm});
            skLineSegment(sketch, "E96", {"start": v(16.96, -1.1) * mm, "end": v(16.96, -0.02) * mm});
            skLineSegment(sketch, "E97", {"start": v(16.96, -0.02) * mm, "end": v(19.78, 4.06) * mm});
            skLineSegment(sketch, "E98", {"start": v(19.78, 4.06) * mm, "end": v(20.83, 4.06) * mm});
            skLineSegment(sketch, "E99", {"start": v(20.83, 4.06) * mm, "end": v(20.83, -0.02) * mm});
            skLineSegment(sketch, "E100", {"start": v(20.83, -0.02) * mm, "end": v(21.64, -0.02) * mm});
            skLineSegment(sketch, "E101", {"start": v(21.64, -0.02) * mm, "end": v(21.64, -1.1) * mm});
            skLineSegment(sketch, "E102", {"start": v(21.64, -1.1) * mm, "end": v(20.83, -1.1) * mm});
            skLineSegment(sketch, "E103", {"start": v(20.83, -1.1) * mm, "end": v(20.83, -2.4) * mm});
            skLineSegment(sketch, "E104", {"start": v(20.83, -2.4) * mm, "end": v(19.62, -2.4) * mm});
            skLineSegment(sketch, "E105", {"start": v(19.62, -0.02) * mm, "end": v(19.62, 2.18) * mm});
            skLineSegment(sketch, "E106", {"start": v(19.62, 2.18) * mm, "end": v(18.13, -0.02) * mm});
            skLineSegment(sketch, "E107", {"start": v(18.13, -0.02) * mm, "end": v(19.62, -0.02) * mm});
            skLineSegment(sketch, "E108", {"start": v(14.66, -10.27) * mm, "end": v(15.9, -10.14) * mm});
            skLineSegment(sketch, "E109", {"start": v(15.83, -9.07) * mm, "end": v(14.81, -8.92) * mm});
            skLineSegment(sketch, "E110", {"start": v(14.81, -8.92) * mm, "end": v(15.45, -5.57) * mm});
            skLineSegment(sketch, "E111", {"start": v(15.45, -5.57) * mm, "end": v(18.75, -5.57) * mm});
            skLineSegment(sketch, "E112", {"start": v(18.75, -5.57) * mm, "end": v(18.75, -6.73) * mm});
            skLineSegment(sketch, "E113", {"start": v(18.75, -6.73) * mm, "end": v(16.4, -6.73) * mm});
            skLineSegment(sketch, "E114", {"start": v(16.4, -6.73) * mm, "end": v(16.2, -7.82) * mm});
            skLineSegment(sketch, "E115", {"start": v(-1.68, 6.99) * mm, "end": v(-5.93, 6.99) * mm});
            skLineSegment(sketch, "E116", {"start": v(-5.93, 6.99) * mm, "end": v(-5.93, 8.4) * mm});
            skLineSegment(sketch, "E117", {"start": v(-5.93, 8.4) * mm, "end": v(-1.68, 8.4) * mm});
            skLineSegment(sketch, "E118", {"start": v(-1.68, -0.1) * mm, "end": v(-5.93, -0.1) * mm});
            skLineSegment(sketch, "E119", {"start": v(-5.93, -0.1) * mm, "end": v(-5.93, 1.32) * mm});
            skLineSegment(sketch, "E120", {"start": v(-5.93, 1.32) * mm, "end": v(-1.68, 1.32) * mm});
            skLineSegment(sketch, "E121", {"start": v(3.93, -2.25) * mm, "end": v(-0.32, -2.25) * mm});
            skLineSegment(sketch, "E122", {"start": v(-0.32, -2.25) * mm, "end": v(-0.32, -0.83) * mm});
            skLineSegment(sketch, "E123", {"start": v(-0.32, -0.83) * mm, "end": v(3.93, -0.83) * mm});
            skLineSegment(sketch, "E124", {"start": v(3.93, -9.33) * mm, "end": v(-0.32, -9.33) * mm});
            skLineSegment(sketch, "E125", {"start": v(-0.32, -9.33) * mm, "end": v(-0.32, -7.91) * mm});
            skLineSegment(sketch, "E126", {"start": v(-0.32, -7.91) * mm, "end": v(3.93, -7.91) * mm});
            skLineSegment(sketch, "E127", {"start": v(-0.56, -16.5) * mm, "end": v(-0.56, -15.34) * mm});
            skLineSegment(sketch, "E128", {"start": v(-0.56, -15.34) * mm, "end": v(3.7, -15.34) * mm});
            skLineSegment(sketch, "E129", {"start": v(3.7, -15.34) * mm, "end": v(3.7, -16.24) * mm});
            skLineSegment(sketch, "E130", {"start": v(1.52, -21.7) * mm, "end": v(0.31, -21.7) * mm});
            skLineSegment(sketch, "E131", {"start": v(2.28, -16.5) * mm, "end": v(-0.56, -16.5) * mm});
            skLineSegment(sketch, "E132", {"start": v(-16.92, -11.85) * mm, "end": v(-15.71, -11.72) * mm});
            skLineSegment(sketch, "E133", {"start": v(-18.78, -3.73) * mm, "end": v(-20.03, -3.73) * mm});
            skLineSegment(sketch, "E134", {"start": v(-20.03, -3.73) * mm, "end": v(-20.03, 0.91) * mm});
            skLineSegment(sketch, "E135", {"start": v(-21.64, -0.02) * mm, "end": v(-21.64, 1.1) * mm});
            skLineSegment(sketch, "E136", {"start": v(-19.8, 2.73) * mm, "end": v(-18.78, 2.73) * mm});
            skLineSegment(sketch, "E137", {"start": v(-18.78, 2.73) * mm, "end": v(-18.78, -3.73) * mm});
            skLineSegment(sketch, "E138", {"start": v(-17.84, 4.43) * mm, "end": v(-19.09, 4.43) * mm});
            skLineSegment(sketch, "E139", {"start": v(-19.09, 4.43) * mm, "end": v(-19.09, 9.08) * mm});
            skLineSegment(sketch, "E140", {"start": v(-20.7, 8.14) * mm, "end": v(-20.7, 9.26) * mm});
            skLineSegment(sketch, "E141", {"start": v(-18.85, 10.9) * mm, "end": v(-17.84, 10.9) * mm});
            skLineSegment(sketch, "E142", {"start": v(-17.84, 10.9) * mm, "end": v(-17.84, 4.43) * mm});
            skLineSegment(sketch, "E143", {"start": v(-13.27, 4.43) * mm, "end": v(-14.52, 4.43) * mm});
            skLineSegment(sketch, "E144", {"start": v(-14.52, 4.43) * mm, "end": v(-14.52, 9.08) * mm});
            skLineSegment(sketch, "E145", {"start": v(-16.13, 8.14) * mm, "end": v(-16.13, 9.26) * mm});
            skLineSegment(sketch, "E146", {"start": v(-14.28, 10.9) * mm, "end": v(-13.27, 10.9) * mm});
            skLineSegment(sketch, "E147", {"start": v(-13.27, 10.9) * mm, "end": v(-13.27, 4.43) * mm});
            skLineSegment(sketch, "E148", {"start": v(-12.44, 11.96) * mm, "end": v(-13.69, 11.96) * mm});
            skLineSegment(sketch, "E149", {"start": v(-13.69, 11.96) * mm, "end": v(-13.69, 16.61) * mm});
            skLineSegment(sketch, "E150", {"start": v(-15.3, 15.68) * mm, "end": v(-15.3, 16.8) * mm});
            skLineSegment(sketch, "E151", {"start": v(-13.45, 18.43) * mm, "end": v(-12.44, 18.43) * mm});
            skLineSegment(sketch, "E152", {"start": v(-12.44, 18.43) * mm, "end": v(-12.44, 11.96) * mm});
            skLineSegment(sketch, "E153", {"start": v(-6.35, 13.11) * mm, "end": v(-6.35, 11.96) * mm});
            skLineSegment(sketch, "E154", {"start": v(-6.35, 11.96) * mm, "end": v(-10.73, 11.96) * mm});
            skLineSegment(sketch, "E155", {"start": v(-9.34, 16.4) * mm, "end": v(-10.58, 16.52) * mm});
            skLineSegment(sketch, "E156", {"start": v(-8.83, 13.11) * mm, "end": v(-6.35, 13.11) * mm});
            skFitSpline(sketch, "E157", {"points": [v(11.62, -14.26) * mm, v(11.59, -14.02) * mm, v(11.51, -13.84) * mm, v(11.39, -13.72) * mm]});
            skFitSpline(sketch, "E158", {"points": [v(11.39, -13.72) * mm, v(11.26, -13.6) * mm, v(11.1, -13.54) * mm, v(10.9, -13.54) * mm]});
            skFitSpline(sketch, "E159", {"points": [v(10.9, -13.54) * mm, v(10.64, -13.54) * mm, v(10.42, -13.66) * mm, v(10.23, -13.9) * mm]});
            skFitSpline(sketch, "E160", {"points": [v(10.23, -13.9) * mm, v(10.05, -14.13) * mm, v(9.94, -14.62) * mm, v(9.9, -15.36) * mm]});
            skFitSpline(sketch, "E161", {"points": [v(9.9, -15.36) * mm, v(10.2, -15) * mm, v(10.59, -14.81) * mm, v(11.05, -14.81) * mm]});
            skFitSpline(sketch, "E162", {"points": [v(11.05, -14.81) * mm, v(11.57, -14.81) * mm, v(12.02, -15) * mm, v(12.39, -15.4) * mm]});
            skFitSpline(sketch, "E163", {"points": [v(12.39, -15.4) * mm, v(12.76, -15.8) * mm, v(12.95, -16.3) * mm, v(12.95, -16.92) * mm]});
            skFitSpline(sketch, "E164", {"points": [v(12.95, -16.92) * mm, v(12.95, -17.58) * mm, v(12.75, -18.1) * mm, v(12.36, -18.5) * mm]});
            skFitSpline(sketch, "E165", {"points": [v(12.36, -18.5) * mm, v(11.97, -18.9) * mm, v(11.47, -19.1) * mm, v(10.85, -19.1) * mm]});
            skFitSpline(sketch, "E166", {"points": [v(10.85, -19.1) * mm, v(10.2, -19.1) * mm, v(9.66, -18.85) * mm, v(9.23, -18.35) * mm]});
            skFitSpline(sketch, "E167", {"points": [v(9.23, -18.35) * mm, v(8.8, -17.84) * mm, v(8.6, -17.01) * mm, v(8.6, -15.86) * mm]});
            skFitSpline(sketch, "E168", {"points": [v(8.6, -15.86) * mm, v(8.6, -14.68) * mm, v(8.82, -13.83) * mm, v(9.26, -13.31) * mm]});
            skFitSpline(sketch, "E169", {"points": [v(9.26, -13.31) * mm, v(9.7, -12.8) * mm, v(10.27, -12.53) * mm, v(10.98, -12.53) * mm]});
            skFitSpline(sketch, "E170", {"points": [v(10.98, -12.53) * mm, v(11.47, -12.53) * mm, v(11.88, -12.67) * mm, v(12.2, -12.94) * mm]});
            skFitSpline(sketch, "E171", {"points": [v(12.2, -12.94) * mm, v(12.53, -13.22) * mm, v(12.74, -13.61) * mm, v(12.83, -14.13) * mm]});
            skFitSpline(sketch, "E172", {"points": [v(10, -16.82) * mm, v(10, -17.22) * mm, v(10.1, -17.53) * mm, v(10.28, -17.75) * mm]});
            skFitSpline(sketch, "E173", {"points": [v(10.28, -17.75) * mm, v(10.46, -17.97) * mm, v(10.68, -18.08) * mm, v(10.92, -18.08) * mm]});
            skFitSpline(sketch, "E174", {"points": [v(10.92, -18.08) * mm, v(11.15, -18.08) * mm, v(11.34, -17.99) * mm, v(11.5, -17.81) * mm]});
            skFitSpline(sketch, "E175", {"points": [v(11.5, -17.81) * mm, v(11.65, -17.63) * mm, v(11.72, -17.34) * mm, v(11.72, -16.93) * mm]});
            skFitSpline(sketch, "E176", {"points": [v(11.72, -16.93) * mm, v(11.72, -16.51) * mm, v(11.64, -16.2) * mm, v(11.48, -16.02) * mm]});
            skFitSpline(sketch, "E177", {"points": [v(11.48, -16.02) * mm, v(11.31, -15.82) * mm, v(11.1, -15.72) * mm, v(10.85, -15.72) * mm]});
            skFitSpline(sketch, "E178", {"points": [v(10.85, -15.72) * mm, v(10.61, -15.72) * mm, v(10.41, -15.82) * mm, v(10.25, -16) * mm]});
            skFitSpline(sketch, "E179", {"points": [v(10.25, -16) * mm, v(10.08, -16.19) * mm, v(10, -16.46) * mm, v(10, -16.82) * mm]});
            skFitSpline(sketch, "E180", {"points": [v(-0.76, 19.88) * mm, v(-1.21, 19.46) * mm, v(-1.75, 19.15) * mm, v(-2.37, 18.94) * mm]});
            skFitSpline(sketch, "E181", {"points": [v(-2.37, 20.06) * mm, v(-2.04, 20.17) * mm, v(-1.69, 20.37) * mm, v(-1.3, 20.66) * mm]});
            skFitSpline(sketch, "E182", {"points": [v(-1.3, 20.66) * mm, v(-0.92, 20.96) * mm, v(-0.66, 21.3) * mm, v(-0.52, 21.7) * mm]});
            skFitSpline(sketch, "E183", {"points": [v(5.87, 13.58) * mm, v(5.92, 14) * mm, v(6.06, 14.42) * mm, v(6.3, 14.8) * mm]});
            skFitSpline(sketch, "E184", {"points": [v(6.3, 14.8) * mm, v(6.53, 15.2) * mm, v(7, 15.7) * mm, v(7.7, 16.35) * mm]});
            skFitSpline(sketch, "E185", {"points": [v(7.7, 16.35) * mm, v(8.26, 16.87) * mm, v(8.6, 17.22) * mm, v(8.73, 17.4) * mm]});
            skFitSpline(sketch, "E186", {"points": [v(8.73, 17.4) * mm, v(8.9, 17.66) * mm, v(9, 17.91) * mm, v(9, 18.16) * mm]});
            skFitSpline(sketch, "E187", {"points": [v(9, 18.16) * mm, v(9, 18.43) * mm, v(8.92, 18.64) * mm, v(8.77, 18.8) * mm]});
            skFitSpline(sketch, "E188", {"points": [v(8.77, 18.8) * mm, v(8.62, 18.94) * mm, v(8.41, 19.01) * mm, v(8.15, 19.01) * mm]});
            skFitSpline(sketch, "E189", {"points": [v(8.15, 19.01) * mm, v(7.89, 19.01) * mm, v(7.68, 18.94) * mm, v(7.53, 18.78) * mm]});
            skFitSpline(sketch, "E190", {"points": [v(7.53, 18.78) * mm, v(7.37, 18.63) * mm, v(7.28, 18.37) * mm, v(7.26, 18) * mm]});
            skFitSpline(sketch, "E191", {"points": [v(6.02, 18.13) * mm, v(6.1, 18.81) * mm, v(6.32, 19.3) * mm, v(6.71, 19.6) * mm]});
            skFitSpline(sketch, "E192", {"points": [v(6.71, 19.6) * mm, v(7.1, 19.89) * mm, v(7.6, 20.04) * mm, v(8.18, 20.04) * mm]});
            skFitSpline(sketch, "E193", {"points": [v(8.18, 20.04) * mm, v(8.82, 20.04) * mm, v(9.33, 19.87) * mm, v(9.7, 19.52) * mm]});
            skFitSpline(sketch, "E194", {"points": [v(9.7, 19.52) * mm, v(10.06, 19.18) * mm, v(10.24, 18.76) * mm, v(10.24, 18.25) * mm]});
            skFitSpline(sketch, "E195", {"points": [v(10.24, 18.25) * mm, v(10.24, 17.96) * mm, v(10.2, 17.68) * mm, v(10.08, 17.42) * mm]});
            skFitSpline(sketch, "E196", {"points": [v(10.08, 17.42) * mm, v(9.98, 17.16) * mm, v(9.82, 16.88) * mm, v(9.59, 16.6) * mm]});
            skFitSpline(sketch, "E197", {"points": [v(9.59, 16.6) * mm, v(9.44, 16.4) * mm, v(9.16, 16.13) * mm, v(8.77, 15.78) * mm]});
            skFitSpline(sketch, "E198", {"points": [v(8.77, 15.78) * mm, v(8.38, 15.42) * mm, v(8.13, 15.18) * mm, v(8.02, 15.06) * mm]});
            skFitSpline(sketch, "E199", {"points": [v(8.02, 15.06) * mm, v(7.92, 14.95) * mm, v(7.83, 14.83) * mm, v(7.77, 14.72) * mm]});
            skFitSpline(sketch, "E200", {"points": [v(15.34, 8.5) * mm, v(15.38, 8.2) * mm, v(15.48, 7.97) * mm, v(15.65, 7.81) * mm]});
            skFitSpline(sketch, "E201", {"points": [v(15.65, 7.81) * mm, v(15.82, 7.65) * mm, v(16.02, 7.57) * mm, v(16.26, 7.57) * mm]});
            skFitSpline(sketch, "E202", {"points": [v(16.26, 7.57) * mm, v(16.52, 7.57) * mm, v(16.73, 7.67) * mm, v(16.9, 7.86) * mm]});
            skFitSpline(sketch, "E203", {"points": [v(16.9, 7.86) * mm, v(17.09, 8.05) * mm, v(17.18, 8.31) * mm, v(17.18, 8.64) * mm]});
            skFitSpline(sketch, "E204", {"points": [v(17.18, 8.64) * mm, v(17.18, 8.95) * mm, v(17.1, 9.2) * mm, v(16.92, 9.38) * mm]});
            skFitSpline(sketch, "E205", {"points": [v(16.92, 9.38) * mm, v(16.75, 9.56) * mm, v(16.55, 9.65) * mm, v(16.3, 9.65) * mm]});
            skFitSpline(sketch, "E206", {"points": [v(16.3, 9.65) * mm, v(16.14, 9.65) * mm, v(15.95, 9.62) * mm, v(15.73, 9.56) * mm]});
            skFitSpline(sketch, "E207", {"points": [v(15.87, 10.56) * mm, v(16.2, 10.55) * mm, v(16.46, 10.63) * mm, v(16.64, 10.78) * mm]});
            skFitSpline(sketch, "E208", {"points": [v(16.64, 10.78) * mm, v(16.82, 10.93) * mm, v(16.9, 11.14) * mm, v(16.9, 11.4) * mm]});
            skFitSpline(sketch, "E209", {"points": [v(16.9, 11.4) * mm, v(16.9, 11.6) * mm, v(16.84, 11.78) * mm, v(16.71, 11.91) * mm]});
            skFitSpline(sketch, "E210", {"points": [v(16.71, 11.91) * mm, v(16.58, 12.04) * mm, v(16.4, 12.1) * mm, v(16.2, 12.1) * mm]});
            skFitSpline(sketch, "E211", {"points": [v(16.2, 12.1) * mm, v(15.98, 12.1) * mm, v(15.8, 12.03) * mm, v(15.65, 11.88) * mm]});
            skFitSpline(sketch, "E212", {"points": [v(15.65, 11.88) * mm, v(15.5, 11.74) * mm, v(15.4, 11.52) * mm, v(15.37, 11.24) * mm]});
            skFitSpline(sketch, "E213", {"points": [v(14.22, 11.44) * mm, v(14.3, 11.83) * mm, v(14.42, 12.14) * mm, v(14.58, 12.37) * mm]});
            skFitSpline(sketch, "E214", {"points": [v(14.58, 12.37) * mm, v(14.74, 12.6) * mm, v(14.97, 12.78) * mm, v(15.26, 12.92) * mm]});
            skFitSpline(sketch, "E215", {"points": [v(15.26, 12.92) * mm, v(15.55, 13.05) * mm, v(15.87, 13.12) * mm, v(16.23, 13.12) * mm]});
            skFitSpline(sketch, "E216", {"points": [v(16.23, 13.12) * mm, v(16.84, 13.12) * mm, v(17.33, 12.92) * mm, v(17.7, 12.54) * mm]});
            skFitSpline(sketch, "E217", {"points": [v(17.7, 12.54) * mm, v(18, 12.22) * mm, v(18.16, 11.87) * mm, v(18.16, 11.47) * mm]});
            skFitSpline(sketch, "E218", {"points": [v(18.16, 11.47) * mm, v(18.16, 10.9) * mm, v(17.85, 10.45) * mm, v(17.22, 10.12) * mm]});
            skFitSpline(sketch, "E219", {"points": [v(17.22, 10.12) * mm, v(17.6, 10.04) * mm, v(17.9, 9.86) * mm, v(18.12, 9.58) * mm]});
            skFitSpline(sketch, "E220", {"points": [v(18.12, 9.58) * mm, v(18.34, 9.3) * mm, v(18.45, 8.98) * mm, v(18.45, 8.59) * mm]});
            skFitSpline(sketch, "E221", {"points": [v(18.45, 8.59) * mm, v(18.45, 8.02) * mm, v(18.25, 7.54) * mm, v(17.83, 7.14) * mm]});
            skFitSpline(sketch, "E222", {"points": [v(17.83, 7.14) * mm, v(17.41, 6.75) * mm, v(16.9, 6.55) * mm, v(16.27, 6.55) * mm]});
            skFitSpline(sketch, "E223", {"points": [v(16.27, 6.55) * mm, v(15.68, 6.55) * mm, v(15.2, 6.71) * mm, v(14.8, 7.05) * mm]});
            skFitSpline(sketch, "E224", {"points": [v(14.8, 7.05) * mm, v(14.42, 7.38) * mm, v(14.2, 7.82) * mm, v(14.13, 8.36) * mm]});
            skFitSpline(sketch, "E225", {"points": [v(15.9, -10.14) * mm, v(15.94, -10.42) * mm, v(16.05, -10.64) * mm, v(16.22, -10.8) * mm]});
            skFitSpline(sketch, "E226", {"points": [v(16.22, -10.8) * mm, v(16.4, -10.96) * mm, v(16.6, -11.04) * mm, v(16.83, -11.04) * mm]});
            skFitSpline(sketch, "E227", {"points": [v(16.83, -11.04) * mm, v(17.09, -11.04) * mm, v(17.3, -10.94) * mm, v(17.49, -10.73) * mm]});
            skFitSpline(sketch, "E228", {"points": [v(17.49, -10.73) * mm, v(17.67, -10.52) * mm, v(17.76, -10.2) * mm, v(17.76, -9.78) * mm]});
            skFitSpline(sketch, "E229", {"points": [v(17.76, -9.78) * mm, v(17.76, -9.39) * mm, v(17.67, -9.1) * mm, v(17.49, -8.9) * mm]});
            skFitSpline(sketch, "E230", {"points": [v(17.49, -8.9) * mm, v(17.3, -8.7) * mm, v(17.08, -8.6) * mm, v(16.8, -8.6) * mm]});
            skFitSpline(sketch, "E231", {"points": [v(16.8, -8.6) * mm, v(16.43, -8.6) * mm, v(16.11, -8.76) * mm, v(15.83, -9.07) * mm]});
            skFitSpline(sketch, "E232", {"points": [v(16.2, -7.82) * mm, v(16.48, -7.68) * mm, v(16.77, -7.62) * mm, v(17.06, -7.62) * mm]});
            skFitSpline(sketch, "E233", {"points": [v(17.06, -7.62) * mm, v(17.61, -7.62) * mm, v(18.08, -7.81) * mm, v(18.46, -8.21) * mm]});
            skFitSpline(sketch, "E234", {"points": [v(18.46, -8.21) * mm, v(18.85, -8.61) * mm, v(19.04, -9.13) * mm, v(19.04, -9.76) * mm]});
            skFitSpline(sketch, "E235", {"points": [v(19.04, -9.76) * mm, v(19.04, -10.3) * mm, v(18.89, -10.76) * mm, v(18.58, -11.18) * mm]});
            skFitSpline(sketch, "E236", {"points": [v(18.58, -11.18) * mm, v(18.15, -11.75) * mm, v(17.56, -12.03) * mm, v(16.81, -12.03) * mm]});
            skFitSpline(sketch, "E237", {"points": [v(16.81, -12.03) * mm, v(16.21, -12.03) * mm, v(15.72, -11.87) * mm, v(15.34, -11.55) * mm]});
            skFitSpline(sketch, "E238", {"points": [v(15.34, -11.55) * mm, v(14.96, -11.23) * mm, v(14.74, -10.8) * mm, v(14.66, -10.27) * mm]});
            skFitSpline(sketch, "E239", {"points": [v(-1.68, 8.4) * mm, v(1.15, 8.4) * mm, v(2.57, 6.99) * mm, v(2.57, 4.16) * mm]});
            skFitSpline(sketch, "E240", {"points": [v(2.57, 4.16) * mm, v(2.57, 1.32) * mm, v(1.15, -0.1) * mm, v(-1.68, -0.1) * mm]});
            skFitSpline(sketch, "E241", {"points": [v(-1.68, 1.32) * mm, v(0.2, 1.32) * mm, v(1.15, 2.27) * mm, v(1.15, 4.16) * mm]});
            skFitSpline(sketch, "E242", {"points": [v(1.15, 4.16) * mm, v(1.15, 6.05) * mm, v(0.2, 6.99) * mm, v(-1.68, 6.99) * mm]});
            skFitSpline(sketch, "E243", {"points": [v(3.93, -0.83) * mm, v(6.76, -0.83) * mm, v(8.18, -2.25) * mm, v(8.18, -5.08) * mm]});
            skFitSpline(sketch, "E244", {"points": [v(8.18, -5.08) * mm, v(8.18, -7.91) * mm, v(6.76, -9.33) * mm, v(3.93, -9.33) * mm]});
            skFitSpline(sketch, "E245", {"points": [v(3.93, -7.91) * mm, v(5.82, -7.91) * mm, v(6.76, -6.97) * mm, v(6.76, -5.08) * mm]});
            skFitSpline(sketch, "E246", {"points": [v(6.76, -5.08) * mm, v(6.76, -3.2) * mm, v(5.82, -2.25) * mm, v(3.93, -2.25) * mm]});
            skFitSpline(sketch, "E247", {"points": [v(3.7, -16.24) * mm, v(3.35, -16.58) * mm, v(3, -17.07) * mm, v(2.63, -17.71) * mm]});
            skFitSpline(sketch, "E248", {"points": [v(2.63, -17.71) * mm, v(2.27, -18.36) * mm, v(1.99, -19.04) * mm, v(1.8, -19.76) * mm]});
            skFitSpline(sketch, "E249", {"points": [v(1.8, -19.76) * mm, v(1.6, -20.48) * mm, v(1.51, -21.12) * mm, v(1.52, -21.7) * mm]});
            skFitSpline(sketch, "E250", {"points": [v(0.31, -21.7) * mm, v(0.33, -20.8) * mm, v(0.52, -19.9) * mm, v(0.87, -18.97) * mm]});
            skFitSpline(sketch, "E251", {"points": [v(0.87, -18.97) * mm, v(1.22, -18.05) * mm, v(1.7, -17.22) * mm, v(2.28, -16.5) * mm]});
            skFitSpline(sketch, "E252", {"points": [v(-8.78, -16.71) * mm, v(-9.1, -16.58) * mm, v(-9.34, -16.4) * mm, v(-9.49, -16.16) * mm]});
            skFitSpline(sketch, "E253", {"points": [v(-9.49, -16.16) * mm, v(-9.63, -15.92) * mm, v(-9.7, -15.66) * mm, v(-9.7, -15.38) * mm]});
            skFitSpline(sketch, "E254", {"points": [v(-9.7, -15.38) * mm, v(-9.7, -14.9) * mm, v(-9.54, -14.5) * mm, v(-9.2, -14.2) * mm]});
            skFitSpline(sketch, "E255", {"points": [v(-9.2, -14.2) * mm, v(-8.86, -13.88) * mm, v(-8.38, -13.72) * mm, v(-7.75, -13.72) * mm]});
            skFitSpline(sketch, "E256", {"points": [v(-7.75, -13.72) * mm, v(-7.13, -13.72) * mm, v(-6.65, -13.88) * mm, v(-6.31, -14.2) * mm]});
            skFitSpline(sketch, "E257", {"points": [v(-6.31, -14.2) * mm, v(-5.97, -14.5) * mm, v(-5.8, -14.9) * mm, v(-5.8, -15.38) * mm]});
            skFitSpline(sketch, "E258", {"points": [v(-5.8, -15.38) * mm, v(-5.8, -15.68) * mm, v(-5.88, -15.95) * mm, v(-6.03, -16.18) * mm]});
            skFitSpline(sketch, "E259", {"points": [v(-6.03, -16.18) * mm, v(-6.2, -16.41) * mm, v(-6.41, -16.59) * mm, v(-6.7, -16.71) * mm]});
            skFitSpline(sketch, "E260", {"points": [v(-6.7, -16.71) * mm, v(-6.34, -16.86) * mm, v(-6.06, -17.07) * mm, v(-5.87, -17.34) * mm]});
            skFitSpline(sketch, "E261", {"points": [v(-5.87, -17.34) * mm, v(-5.69, -17.62) * mm, v(-5.6, -17.93) * mm, v(-5.6, -18.3) * mm]});
            skFitSpline(sketch, "E262", {"points": [v(-5.6, -18.3) * mm, v(-5.6, -18.89) * mm, v(-5.78, -19.37) * mm, v(-6.17, -19.74) * mm]});
            skFitSpline(sketch, "E263", {"points": [v(-6.17, -19.74) * mm, v(-6.55, -20.11) * mm, v(-7.06, -20.3) * mm, v(-7.7, -20.3) * mm]});
            skFitSpline(sketch, "E264", {"points": [v(-7.7, -20.3) * mm, v(-8.29, -20.3) * mm, v(-8.78, -20.14) * mm, v(-9.17, -19.84) * mm]});
            skFitSpline(sketch, "E265", {"points": [v(-9.17, -19.84) * mm, v(-9.64, -19.47) * mm, v(-9.87, -18.98) * mm, v(-9.87, -18.35) * mm]});
            skFitSpline(sketch, "E266", {"points": [v(-9.87, -18.35) * mm, v(-9.87, -18) * mm, v(-9.78, -17.68) * mm, v(-9.6, -17.39) * mm]});
            skFitSpline(sketch, "E267", {"points": [v(-9.6, -17.39) * mm, v(-9.43, -17.1) * mm, v(-9.16, -16.87) * mm, v(-8.78, -16.71) * mm]});
            skFitSpline(sketch, "E268", {"points": [v(-8.53, -15.47) * mm, v(-8.53, -15.72) * mm, v(-8.46, -15.9) * mm, v(-8.32, -16.05) * mm]});
            skFitSpline(sketch, "E269", {"points": [v(-8.32, -16.05) * mm, v(-8.18, -16.18) * mm, v(-7.99, -16.25) * mm, v(-7.75, -16.25) * mm]});
            skFitSpline(sketch, "E270", {"points": [v(-7.75, -16.25) * mm, v(-7.52, -16.25) * mm, v(-7.33, -16.18) * mm, v(-7.18, -16.05) * mm]});
            skFitSpline(sketch, "E271", {"points": [v(-7.18, -16.05) * mm, v(-7.04, -15.9) * mm, v(-6.97, -15.71) * mm, v(-6.97, -15.47) * mm]});
            skFitSpline(sketch, "E272", {"points": [v(-6.97, -15.47) * mm, v(-6.97, -15.23) * mm, v(-7.04, -15.05) * mm, v(-7.18, -14.91) * mm]});
            skFitSpline(sketch, "E273", {"points": [v(-7.18, -14.91) * mm, v(-7.32, -14.77) * mm, v(-7.5, -14.7) * mm, v(-7.74, -14.7) * mm]});
            skFitSpline(sketch, "E274", {"points": [v(-7.74, -14.7) * mm, v(-7.98, -14.7) * mm, v(-8.17, -14.77) * mm, v(-8.31, -14.91) * mm]});
            skFitSpline(sketch, "E275", {"points": [v(-8.31, -14.91) * mm, v(-8.45, -15.05) * mm, v(-8.53, -15.24) * mm, v(-8.53, -15.47) * mm]});
            skFitSpline(sketch, "E276", {"points": [v(-8.64, -18.23) * mm, v(-8.64, -18.57) * mm, v(-8.55, -18.83) * mm, v(-8.38, -19.02) * mm]});
            skFitSpline(sketch, "E277", {"points": [v(-8.38, -19.02) * mm, v(-8.2, -19.21) * mm, v(-7.98, -19.3) * mm, v(-7.72, -19.3) * mm]});
            skFitSpline(sketch, "E278", {"points": [v(-7.72, -19.3) * mm, v(-7.46, -19.3) * mm, v(-7.25, -19.22) * mm, v(-7.08, -19.03) * mm]});
            skFitSpline(sketch, "E279", {"points": [v(-7.08, -19.03) * mm, v(-6.9, -18.85) * mm, v(-6.83, -18.59) * mm, v(-6.83, -18.24) * mm]});
            skFitSpline(sketch, "E280", {"points": [v(-6.83, -18.24) * mm, v(-6.83, -17.94) * mm, v(-6.91, -17.7) * mm, v(-7.08, -17.52) * mm]});
            skFitSpline(sketch, "E281", {"points": [v(-7.08, -17.52) * mm, v(-7.25, -17.33) * mm, v(-7.47, -17.24) * mm, v(-7.74, -17.24) * mm]});
            skFitSpline(sketch, "E282", {"points": [v(-7.74, -17.24) * mm, v(-8.04, -17.24) * mm, v(-8.27, -17.34) * mm, v(-8.42, -17.55) * mm]});
            skFitSpline(sketch, "E283", {"points": [v(-8.42, -17.55) * mm, v(-8.57, -17.76) * mm, v(-8.64, -17.98) * mm, v(-8.64, -18.23) * mm]});
            skFitSpline(sketch, "E284", {"points": [v(-15.71, -11.72) * mm, v(-15.68, -11.96) * mm, v(-15.6, -12.14) * mm, v(-15.48, -12.26) * mm]});
            skFitSpline(sketch, "E285", {"points": [v(-15.48, -12.26) * mm, v(-15.36, -12.38) * mm, v(-15.2, -12.44) * mm, v(-15, -12.44) * mm]});
            skFitSpline(sketch, "E286", {"points": [v(-15, -12.44) * mm, v(-14.73, -12.44) * mm, v(-14.51, -12.32) * mm, v(-14.33, -12.08) * mm]});
            skFitSpline(sketch, "E287", {"points": [v(-14.33, -12.08) * mm, v(-14.15, -11.85) * mm, v(-14.04, -11.37) * mm, v(-13.99, -10.63) * mm]});
            skFitSpline(sketch, "E288", {"points": [v(-13.99, -10.63) * mm, v(-14.3, -10.99) * mm, v(-14.7, -11.17) * mm, v(-15.16, -11.17) * mm]});
            skFitSpline(sketch, "E289", {"points": [v(-15.16, -11.17) * mm, v(-15.68, -11.17) * mm, v(-16.12, -10.97) * mm, v(-16.5, -10.58) * mm]});
            skFitSpline(sketch, "E290", {"points": [v(-16.5, -10.58) * mm, v(-16.86, -10.2) * mm, v(-17.05, -9.68) * mm, v(-17.05, -9.06) * mm]});
            skFitSpline(sketch, "E291", {"points": [v(-17.05, -9.06) * mm, v(-17.05, -8.4) * mm, v(-16.85, -7.88) * mm, v(-16.46, -7.48) * mm]});
            skFitSpline(sketch, "E292", {"points": [v(-16.46, -7.48) * mm, v(-16.07, -7.08) * mm, v(-15.57, -6.88) * mm, v(-14.96, -6.88) * mm]});
            skFitSpline(sketch, "E293", {"points": [v(-14.96, -6.88) * mm, v(-14.3, -6.88) * mm, v(-13.76, -7.13) * mm, v(-13.33, -7.64) * mm]});
            skFitSpline(sketch, "E294", {"points": [v(-13.33, -7.64) * mm, v(-12.91, -8.14) * mm, v(-12.7, -8.97) * mm, v(-12.7, -10.13) * mm]});
            skFitSpline(sketch, "E295", {"points": [v(-12.7, -10.13) * mm, v(-12.7, -11.3) * mm, v(-12.92, -12.15) * mm, v(-13.36, -12.67) * mm]});
            skFitSpline(sketch, "E296", {"points": [v(-13.36, -12.67) * mm, v(-13.8, -13.2) * mm, v(-14.38, -13.45) * mm, v(-15.08, -13.45) * mm]});
            skFitSpline(sketch, "E297", {"points": [v(-15.08, -13.45) * mm, v(-15.6, -13.45) * mm, v(-16, -13.32) * mm, v(-16.32, -13.05) * mm]});
            skFitSpline(sketch, "E298", {"points": [v(-16.32, -13.05) * mm, v(-16.63, -12.79) * mm, v(-16.83, -12.38) * mm, v(-16.92, -11.85) * mm]});
            skFitSpline(sketch, "E299", {"points": [v(-14.1, -9.16) * mm, v(-14.1, -8.76) * mm, v(-14.2, -8.45) * mm, v(-14.38, -8.23) * mm]});
            skFitSpline(sketch, "E300", {"points": [v(-14.38, -8.23) * mm, v(-14.56, -8.01) * mm, v(-14.77, -7.9) * mm, v(-15.02, -7.9) * mm]});
            skFitSpline(sketch, "E301", {"points": [v(-15.02, -7.9) * mm, v(-15.25, -7.9) * mm, v(-15.44, -8) * mm, v(-15.6, -8.17) * mm]});
            skFitSpline(sketch, "E302", {"points": [v(-15.6, -8.17) * mm, v(-15.75, -8.35) * mm, v(-15.82, -8.65) * mm, v(-15.82, -9.06) * mm]});
            skFitSpline(sketch, "E303", {"points": [v(-15.82, -9.06) * mm, v(-15.82, -9.47) * mm, v(-15.74, -9.78) * mm, v(-15.57, -9.97) * mm]});
            skFitSpline(sketch, "E304", {"points": [v(-15.57, -9.97) * mm, v(-15.4, -10.17) * mm, v(-15.2, -10.26) * mm, v(-14.95, -10.26) * mm]});
            skFitSpline(sketch, "E305", {"points": [v(-14.95, -10.26) * mm, v(-14.71, -10.26) * mm, v(-14.5, -10.17) * mm, v(-14.35, -9.98) * mm]});
            skFitSpline(sketch, "E306", {"points": [v(-14.35, -9.98) * mm, v(-14.18, -9.8) * mm, v(-14.1, -9.52) * mm, v(-14.1, -9.16) * mm]});
            skFitSpline(sketch, "E307", {"points": [v(-20.03, 0.91) * mm, v(-20.48, 0.5) * mm, v(-21.02, 0.18) * mm, v(-21.64, -0.02) * mm]});
            skFitSpline(sketch, "E308", {"points": [v(-21.64, 1.1) * mm, v(-21.31, 1.2) * mm, v(-20.96, 1.4) * mm, v(-20.58, 1.7) * mm]});
            skFitSpline(sketch, "E309", {"points": [v(-20.58, 1.7) * mm, v(-20.2, 2) * mm, v(-19.93, 2.34) * mm, v(-19.8, 2.73) * mm]});
            skFitSpline(sketch, "E310", {"points": [v(-14.8, 2.73) * mm, v(-14.17, 2.73) * mm, v(-13.68, 2.5) * mm, v(-13.32, 2.06) * mm]});
            skFitSpline(sketch, "E311", {"points": [v(-13.32, 2.06) * mm, v(-12.9, 1.53) * mm, v(-12.69, 0.66) * mm, v(-12.69, -0.56) * mm]});
            skFitSpline(sketch, "E312", {"points": [v(-12.69, -0.56) * mm, v(-12.69, -1.78) * mm, v(-12.9, -2.65) * mm, v(-13.33, -3.18) * mm]});
            skFitSpline(sketch, "E313", {"points": [v(-13.33, -3.18) * mm, v(-13.68, -3.62) * mm, v(-14.17, -3.84) * mm, v(-14.8, -3.84) * mm]});
            skFitSpline(sketch, "E314", {"points": [v(-14.8, -3.84) * mm, v(-15.43, -3.84) * mm, v(-15.94, -3.6) * mm, v(-16.33, -3.12) * mm]});
            skFitSpline(sketch, "E315", {"points": [v(-16.33, -3.12) * mm, v(-16.72, -2.64) * mm, v(-16.91, -1.78) * mm, v(-16.91, -0.55) * mm]});
            skFitSpline(sketch, "E316", {"points": [v(-16.91, -0.55) * mm, v(-16.91, 0.66) * mm, v(-16.7, 1.54) * mm, v(-16.27, 2.07) * mm]});
            skFitSpline(sketch, "E317", {"points": [v(-16.27, 2.07) * mm, v(-15.92, 2.5) * mm, v(-15.43, 2.73) * mm, v(-14.8, 2.73) * mm]});
            skFitSpline(sketch, "E318", {"points": [v(-14.8, 1.7) * mm, v(-14.95, 1.7) * mm, v(-15.09, 1.66) * mm, v(-15.2, 1.56) * mm]});
            skFitSpline(sketch, "E319", {"points": [v(-15.2, 1.56) * mm, v(-15.32, 1.47) * mm, v(-15.41, 1.3) * mm, v(-15.48, 1.05) * mm]});
            skFitSpline(sketch, "E320", {"points": [v(-15.48, 1.05) * mm, v(-15.57, 0.73) * mm, v(-15.6, 0.2) * mm, v(-15.6, -0.56) * mm]});
            skFitSpline(sketch, "E321", {"points": [v(-15.6, -0.56) * mm, v(-15.6, -1.31) * mm, v(-15.57, -1.83) * mm, v(-15.5, -2.12) * mm]});
            skFitSpline(sketch, "E322", {"points": [v(-15.5, -2.12) * mm, v(-15.42, -2.4) * mm, v(-15.32, -2.59) * mm, v(-15.2, -2.68) * mm]});
            skFitSpline(sketch, "E323", {"points": [v(-15.2, -2.68) * mm, v(-15.09, -2.77) * mm, v(-14.95, -2.82) * mm, v(-14.8, -2.82) * mm]});
            skFitSpline(sketch, "E324", {"points": [v(-14.8, -2.82) * mm, v(-14.65, -2.82) * mm, v(-14.51, -2.77) * mm, v(-14.4, -2.68) * mm]});
            skFitSpline(sketch, "E325", {"points": [v(-14.4, -2.68) * mm, v(-14.28, -2.58) * mm, v(-14.19, -2.41) * mm, v(-14.12, -2.17) * mm]});
            skFitSpline(sketch, "E326", {"points": [v(-14.12, -2.17) * mm, v(-14.03, -1.85) * mm, v(-14, -1.31) * mm, v(-14, -0.56) * mm]});
            skFitSpline(sketch, "E327", {"points": [v(-14, -0.56) * mm, v(-14, 0.2) * mm, v(-14.03, 0.71) * mm, v(-14.1, 1) * mm]});
            skFitSpline(sketch, "E328", {"points": [v(-14.1, 1) * mm, v(-14.18, 1.28) * mm, v(-14.28, 1.47) * mm, v(-14.4, 1.56) * mm]});
            skFitSpline(sketch, "E329", {"points": [v(-14.4, 1.56) * mm, v(-14.52, 1.66) * mm, v(-14.65, 1.7) * mm, v(-14.8, 1.7) * mm]});
            skFitSpline(sketch, "E330", {"points": [v(-19.09, 9.08) * mm, v(-19.54, 8.66) * mm, v(-20.08, 8.34) * mm, v(-20.7, 8.14) * mm]});
            skFitSpline(sketch, "E331", {"points": [v(-20.7, 9.26) * mm, v(-20.37, 9.37) * mm, v(-20.02, 9.57) * mm, v(-19.64, 9.86) * mm]});
            skFitSpline(sketch, "E332", {"points": [v(-19.64, 9.86) * mm, v(-19.25, 10.15) * mm, v(-19, 10.5) * mm, v(-18.85, 10.9) * mm]});
            skFitSpline(sketch, "E333", {"points": [v(-14.52, 9.08) * mm, v(-14.98, 8.66) * mm, v(-15.51, 8.34) * mm, v(-16.13, 8.14) * mm]});
            skFitSpline(sketch, "E334", {"points": [v(-16.13, 9.26) * mm, v(-15.8, 9.37) * mm, v(-15.45, 9.57) * mm, v(-15.07, 9.86) * mm]});
            skFitSpline(sketch, "E335", {"points": [v(-15.07, 9.86) * mm, v(-14.69, 10.15) * mm, v(-14.43, 10.5) * mm, v(-14.28, 10.9) * mm]});
            skFitSpline(sketch, "E336", {"points": [v(-13.69, 16.61) * mm, v(-14.14, 16.2) * mm, v(-14.68, 15.88) * mm, v(-15.3, 15.68) * mm]});
            skFitSpline(sketch, "E337", {"points": [v(-15.3, 16.8) * mm, v(-14.97, 16.9) * mm, v(-14.62, 17.1) * mm, v(-14.24, 17.4) * mm]});
            skFitSpline(sketch, "E338", {"points": [v(-14.24, 17.4) * mm, v(-13.85, 17.69) * mm, v(-13.6, 18.03) * mm, v(-13.45, 18.43) * mm]});
            skFitSpline(sketch, "E339", {"points": [v(-10.73, 11.96) * mm, v(-10.68, 12.4) * mm, v(-10.54, 12.8) * mm, v(-10.3, 13.2) * mm]});
            skFitSpline(sketch, "E340", {"points": [v(-10.3, 13.2) * mm, v(-10.06, 13.58) * mm, v(-9.6, 14.1) * mm, v(-8.9, 14.74) * mm]});
            skFitSpline(sketch, "E341", {"points": [v(-8.9, 14.74) * mm, v(-8.34, 15.26) * mm, v(-8, 15.6) * mm, v(-7.86, 15.8) * mm]});
            skFitSpline(sketch, "E342", {"points": [v(-7.86, 15.8) * mm, v(-7.7, 16.05) * mm, v(-7.6, 16.3) * mm, v(-7.6, 16.55) * mm]});
            skFitSpline(sketch, "E343", {"points": [v(-7.6, 16.55) * mm, v(-7.6, 16.82) * mm, v(-7.68, 17.03) * mm, v(-7.83, 17.18) * mm]});
            skFitSpline(sketch, "E344", {"points": [v(-7.83, 17.18) * mm, v(-7.98, 17.33) * mm, v(-8.19, 17.4) * mm, v(-8.45, 17.4) * mm]});
            skFitSpline(sketch, "E345", {"points": [v(-8.45, 17.4) * mm, v(-8.71, 17.4) * mm, v(-8.92, 17.33) * mm, v(-9.07, 17.17) * mm]});
            skFitSpline(sketch, "E346", {"points": [v(-9.07, 17.17) * mm, v(-9.23, 17.02) * mm, v(-9.31, 16.76) * mm, v(-9.34, 16.4) * mm]});
            skFitSpline(sketch, "E347", {"points": [v(-10.58, 16.52) * mm, v(-10.5, 17.2) * mm, v(-10.27, 17.69) * mm, v(-9.88, 17.98) * mm]});
            skFitSpline(sketch, "E348", {"points": [v(-9.88, 17.98) * mm, v(-9.5, 18.28) * mm, v(-9, 18.43) * mm, v(-8.42, 18.43) * mm]});
            skFitSpline(sketch, "E349", {"points": [v(-8.42, 18.43) * mm, v(-7.78, 18.43) * mm, v(-7.27, 18.25) * mm, v(-6.9, 17.91) * mm]});
            skFitSpline(sketch, "E350", {"points": [v(-6.9, 17.91) * mm, v(-6.54, 17.57) * mm, v(-6.35, 17.14) * mm, v(-6.35, 16.63) * mm]});
            skFitSpline(sketch, "E351", {"points": [v(-6.35, 16.63) * mm, v(-6.35, 16.34) * mm, v(-6.4, 16.07) * mm, v(-6.51, 15.8) * mm]});
            skFitSpline(sketch, "E352", {"points": [v(-6.51, 15.8) * mm, v(-6.62, 15.54) * mm, v(-6.78, 15.27) * mm, v(-7.01, 14.98) * mm]});
            skFitSpline(sketch, "E353", {"points": [v(-7.01, 14.98) * mm, v(-7.16, 14.8) * mm, v(-7.43, 14.52) * mm, v(-7.83, 14.16) * mm]});
            skFitSpline(sketch, "E354", {"points": [v(-7.83, 14.16) * mm, v(-8.22, 13.8) * mm, v(-8.47, 13.57) * mm, v(-8.58, 13.45) * mm]});
            skFitSpline(sketch, "E355", {"points": [v(-8.58, 13.45) * mm, v(-8.68, 13.34) * mm, v(-8.77, 13.22) * mm, v(-8.83, 13.11) * mm]});
            skSolve(sketch);
        }
        {
            var Q0;
            Q0 = qSketchRegion(id + "F32", true);
            extrude(context, id + "F33", {"entities" : qUnion([Q0]), "operationType" : NewBodyOperationType.ADD, "depth" : 1 * mm, "offsetDistance" : 25 * mm});
        }
        {
            var Q0;
            Q0=makeQuery(id+"F31.opExtrude","CAP_FACE",FACE,{"disambiguationData":[OSD([sQuery(id+"F30.wireOp",EDGE,"E73"),sQuery(id+"F30.wireOp",EDGE,"E74"),sQuery(id+"F30.wireOp",EDGE,"E77"),sQuery(id+"F30.wireOp",EDGE,"E78.trimOffspring")])],"isStart":true});
            fillet(context, id + "F34", {"entities" : qUnion([Q0]), "radius" : 1 * mm, "tangentPropagation" : true, "allowEdgeOverflow" : false});
        }
    });
